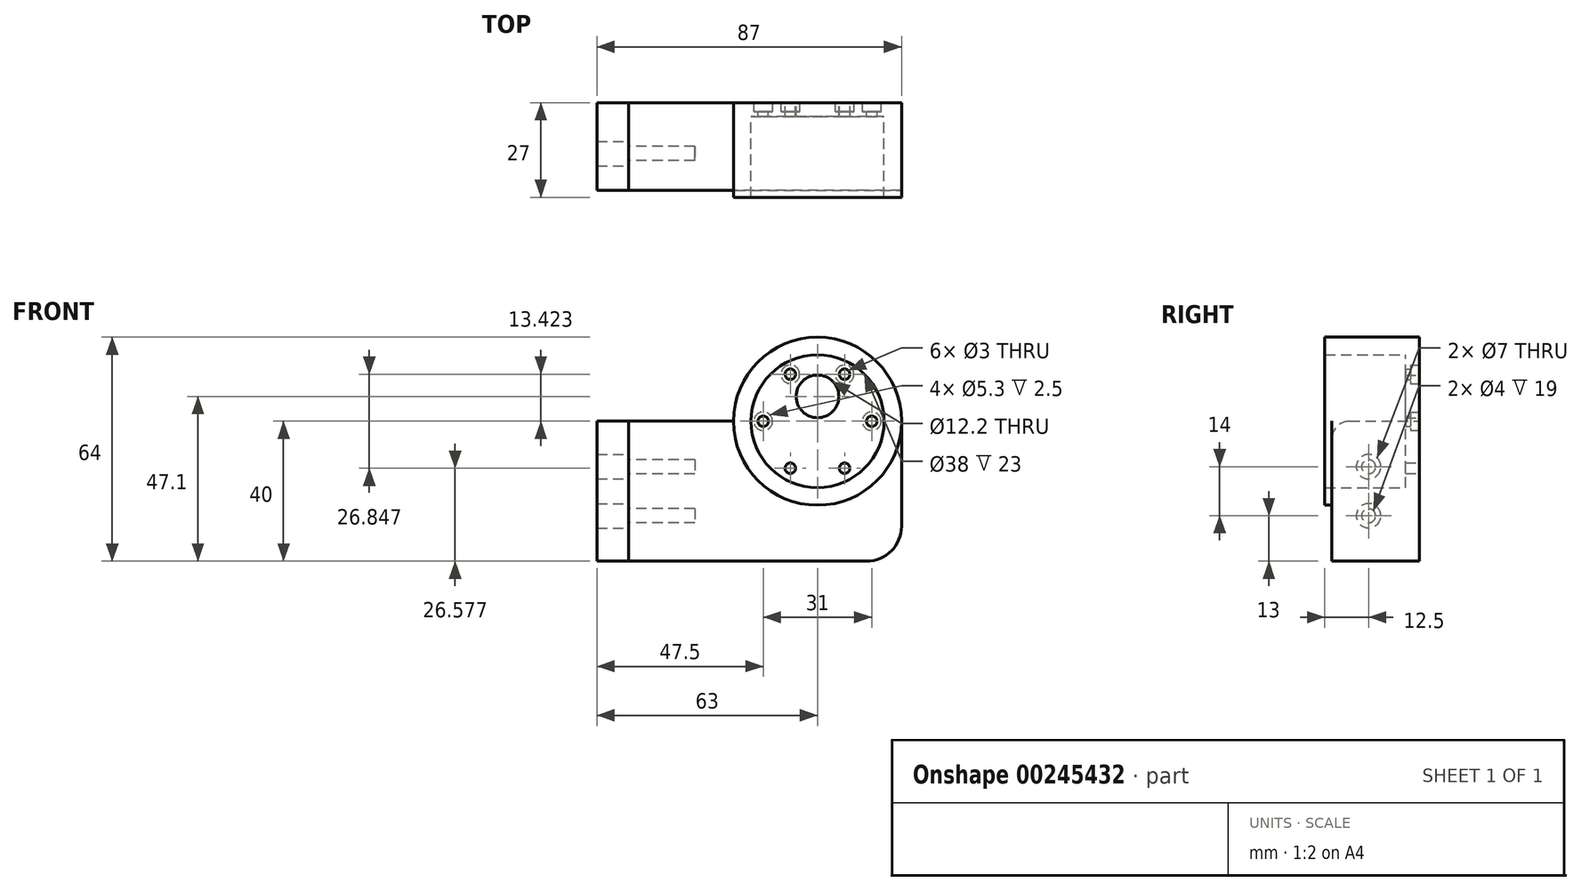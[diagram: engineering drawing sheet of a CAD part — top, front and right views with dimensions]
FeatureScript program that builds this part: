
annotation { "Feature Type Name" : "Feature", "Feature Type Description" : "" }
export const myFeature = defineFeature(function(context is Context, id is Id, definition is map)
    precondition{}
    {
        {
            var Q0;
            Q0=qCreatedBy(makeId("Front.planeOp"),FACE);
            var sketch = newSketch(context, id + "F0", { "sketchPlane" : qUnion([Q0])});
            skCircle(sketch, "E0", {"center": v(0, 0) * mm, "radius": 19 * mm});
            skCircle(sketch, "E1", {"center": v(0, 7.1) * mm, "radius": 6.1 * mm});
            skLineSegment(sketch, "E2", {"start": v(0, 0) * mm, "end": v(15.5, 0) * mm});
            skCircle(sketch, "E3", {"center": v(15.5, 0) * mm, "radius": 1.5 * mm});
            skCircle(sketch, "E4.1.0", {"center": v(7.75, 13.42) * mm, "radius": 1.5 * mm});
            skCircle(sketch, "E4.2.0", {"center": v(-7.75, 13.42) * mm, "radius": 1.5 * mm});
            skCircle(sketch, "E4.3.0", {"center": v(-15.5, 0) * mm, "radius": 1.5 * mm});
            skCircle(sketch, "E4.4.0", {"center": v(-7.75, -13.42) * mm, "radius": 1.5 * mm});
            skCircle(sketch, "E4.5.0", {"center": v(7.75, -13.42) * mm, "radius": 1.5 * mm});
            skSolve(sketch);
        }
        {
            var Q0;
            Q0=qSketchRegion(id+"F0",true);
            extrude(context, id + "F1", {"entities" : qUnion([Q0]), "depth" : 4 * mm});
        }
        {
            var Q0;
            Q0=qCreatedBy(makeId("Front.planeOp"),FACE);
            var sketch = newSketch(context, id + "F2", { "sketchPlane" : qUnion([Q0])});
            skCircle(sketch, "E5", {"center": v(0, 0) * mm, "radius": 19 * mm});
            skCircle(sketch, "E6", {"center": v(0, 0) * mm, "radius": 24 * mm});
            skSolve(sketch);
        }
        {
            var Q0;
            Q0=qSketchRegion(id+"F2",true);
            extrude(context, id + "F3", {"entities" : qUnion([Q0]), "operationType" : NewBodyOperationType.ADD, "depth" : 27 * mm});
        }
        {
            var Q0;
            Q0=makeQuery(id+"F3.boolean.opBoolean","MERGE",FACE,{"derivedFrom":[makeQuery(id+"F1.opExtrude","CAP_FACE",FACE,{"disambiguationData":[OSD([sQuery(id+"F0.wireOp",EDGE,"E0"),sQuery(id+"F0.wireOp",EDGE,"E1"),sQuery(id+"F0.wireOp",EDGE,"E3"),sQuery(id+"F0.wireOp",EDGE,"E4.1.0"),sQuery(id+"F0.wireOp",EDGE,"E4.2.0"),sQuery(id+"F0.wireOp",EDGE,"E4.3.0"),sQuery(id+"F0.wireOp",EDGE,"E4.4.0"),sQuery(id+"F0.wireOp",EDGE,"E4.5.0")])],"isStart":true}),makeQuery(id+"F3.opExtrude","CAP_FACE",FACE,{"disambiguationData":[OSD([sQuery(id+"F2.wireOp",EDGE,"E5"),sQuery(id+"F2.wireOp",EDGE,"E6")])],"isStart":true})]});
            var sketch = newSketch(context, id + "F4", { "sketchPlane" : qUnion([Q0])});
            skLineSegment(sketch, "E7", {"start": v(24, 0) * mm, "end": v(24, -40) * mm});
            skLineSegment(sketch, "E8", {"start": v(24, -40) * mm, "end": v(0, -40) * mm});
            skLineSegment(sketch, "E9", {"start": v(-24, 0) * mm, "end": v(-24, -40) * mm});
            skLineSegment(sketch, "E10", {"start": v(-24, -40) * mm, "end": v(0, -40) * mm});
            skArc(sketch, "E11", {"start": v(-24, 0) * mm, "mid": v(0, -24) * mm, "end": v(24, 0) * mm});
            skSolve(sketch);
        }
        {
            var Q0;
            Q0=qSketchRegion(id+"F4",true);
            extrude(context, id + "F5", {"entities" : qUnion([Q0]), "operationType" : NewBodyOperationType.ADD, "oppositeDirection" : true, "depth" : 25 * mm});
        }
        {
            var Q0;
            Q0=makeQuery(id+"F5.boolean.opBoolean","MERGE",FACE,{"derivedFrom":[makeQuery(id+"F3.boolean.opBoolean","MERGE",FACE,{"derivedFrom":[makeQuery(id+"F1.opExtrude","CAP_FACE",FACE,{"disambiguationData":[OSD([sQuery(id+"F0.wireOp",EDGE,"E0"),sQuery(id+"F0.wireOp",EDGE,"E1"),sQuery(id+"F0.wireOp",EDGE,"E3"),sQuery(id+"F0.wireOp",EDGE,"E4.1.0"),sQuery(id+"F0.wireOp",EDGE,"E4.2.0"),sQuery(id+"F0.wireOp",EDGE,"E4.3.0"),sQuery(id+"F0.wireOp",EDGE,"E4.4.0"),sQuery(id+"F0.wireOp",EDGE,"E4.5.0")])],"isStart":true}),makeQuery(id+"F3.opExtrude","CAP_FACE",FACE,{"disambiguationData":[OSD([sQuery(id+"F2.wireOp",EDGE,"E5"),sQuery(id+"F2.wireOp",EDGE,"E6")])],"isStart":true})]}),makeQuery(id+"F5.opExtrude","CAP_FACE",FACE,{"disambiguationData":[OSD([sQuery(id+"F4.wireOp",EDGE,"E7"),sQuery(id+"F4.wireOp",EDGE,"E8"),sQuery(id+"F4.wireOp",EDGE,"E9"),sQuery(id+"F4.wireOp",EDGE,"E10"),sQuery(id+"F4.wireOp",EDGE,"E11")])],"isStart":true})]});
            var sketch = newSketch(context, id + "F6", { "sketchPlane" : qUnion([Q0])});
            skCircle(sketch, "E12", {"center": v(-7.75, 13.42) * mm, "radius": 2.65 * mm});
            skCircle(sketch, "E13", {"center": v(7.75, 13.42) * mm, "radius": 2.65 * mm});
            skCircle(sketch, "E14", {"center": v(-15.5, 0) * mm, "radius": 2.65 * mm});
            skCircle(sketch, "E15", {"center": v(15.5, 0) * mm, "radius": 2.65 * mm});
            skSolve(sketch);
        }
        {
            var Q0;
            Q0=qSketchRegion(id+"F6",true);
            extrude(context, id + "F7", {"entities" : qUnion([Q0]), "operationType" : NewBodyOperationType.REMOVE, "oppositeDirection" : true, "depth" : 2.5 * mm});
        }
        {
            var Q0;
            Q0=makeQuery(id+"F5.opExtrude","SWEPT_FACE",FACE,{"disambiguationData":[OSD([sQuery(id+"F4.wireOp",EDGE,"E7")])]});
            var sketch = newSketch(context, id + "F8", { "sketchPlane" : qUnion([Q0])});
            skLineSegment(sketch, "E16.bottom", {"start": v(0, 0) * mm, "end": v(25, 0) * mm});
            skLineSegment(sketch, "E16.top", {"start": v(0, -40) * mm, "end": v(25, -40) * mm});
            skLineSegment(sketch, "E16.left", {"start": v(0, 0) * mm, "end": v(0, -40) * mm});
            skLineSegment(sketch, "E16.right", {"start": v(25, 0) * mm, "end": v(25, -40) * mm});
            skSolve(sketch);
        }
        {
            var Q0;
            Q0=qSketchRegion(id+"F8",true);
            extrude(context, id + "F9", {"entities" : qUnion([Q0]), "operationType" : NewBodyOperationType.ADD, "depth" : 30 * mm});
        }
        {
            var Q0;
            Q0=makeQuery(id+"F9.opExtrude","SWEPT_EDGE",EDGE,{"disambiguationData":[OSD([sQuery(id+"F8.wireOp",EDGE,"E16.bottom"),sQuery(id+"F8.wireOp",EDGE,"E16.right")])]});
            fillet(context, id + "F10", {"entities" : qUnion([Q0]), "radius" : 5 * mm, "tangentPropagation" : true, "allowEdgeOverflow" : false});
        }
        {
            var Q0;
            Q0=makeQuery(id+"F5.opExtrude","SWEPT_EDGE",EDGE,{"disambiguationData":[OSD([sQuery(id+"F4.wireOp",EDGE,"E9"),sQuery(id+"F4.wireOp",EDGE,"E10")])]});
            fillet(context, id + "F11", {"entities" : qUnion([Q0]), "radius" : 10 * mm, "tangentPropagation" : true, "allowEdgeOverflow" : false});
        }
        {
            var Q0;
            Q0=makeQuery(id+"F9.opExtrude","CAP_FACE",FACE,{"disambiguationData":[OSD([sQuery(id+"F8.wireOp",EDGE,"E16.bottom"),sQuery(id+"F8.wireOp",EDGE,"E16.top"),sQuery(id+"F8.wireOp",EDGE,"E16.left"),sQuery(id+"F8.wireOp",EDGE,"E16.right")])],"isStart":false});
            var sketch = newSketch(context, id + "F12", { "sketchPlane" : qUnion([Q0])});
            skLineSegment(sketch, "E17", {"start": v(25, -40) * mm, "end": v(4, -40) * mm});
            skLineSegment(sketch, "E18", {"start": v(14.5, -40) * mm, "end": v(14.5, 0) * mm});
            skLineSegment(sketch, "E19", {"start": v(14.5, 0) * mm, "end": v(14.5, -13) * mm});
            skLineSegment(sketch, "E20", {"start": v(14.5, -40) * mm, "end": v(14.5, -27) * mm});
            skCircle(sketch, "E21", {"center": v(14.5, -13) * mm, "radius": 2 * mm});
            skCircle(sketch, "E22", {"center": v(14.5, -27) * mm, "radius": 2 * mm});
            skSolve(sketch);
        }
        {
            var Q0;
            Q0=qSketchRegion(id+"F12",true);
            extrude(context, id + "F13", {"entities" : qUnion([Q0]), "operationType" : NewBodyOperationType.REMOVE, "oppositeDirection" : true, "depth" : 19 * mm});
        }
        {
            var Q0;
            Q0=makeQuery(id+"F9.opExtrude","CAP_FACE",FACE,{"disambiguationData":[OSD([sQuery(id+"F8.wireOp",EDGE,"E16.bottom"),sQuery(id+"F8.wireOp",EDGE,"E16.top"),sQuery(id+"F8.wireOp",EDGE,"E16.left"),sQuery(id+"F8.wireOp",EDGE,"E16.right")])],"isStart":false});
            var sketch = newSketch(context, id + "F14", { "sketchPlane" : qUnion([Q0])});
            skLineSegment(sketch, "E23.0", {"start": v(0, 0) * mm, "end": v(0, -40) * mm});
            skLineSegment(sketch, "E24.0", {"start": v(25, -5) * mm, "end": v(25, -40) * mm});
            skArc(sketch, "E25.0", {"start": v(25, -5) * mm, "mid": v(23.54, -1.46) * mm, "end": v(20, 0) * mm});
            skLineSegment(sketch, "E26.0", {"start": v(20, 0) * mm, "end": v(0, 0) * mm});
            skLineSegment(sketch, "E27.0", {"start": v(25, -40) * mm, "end": v(0, -40) * mm});
            skCircle(sketch, "E28", {"center": v(14.5, -13) * mm, "radius": 3.5 * mm});
            skCircle(sketch, "E29", {"center": v(14.5, -27) * mm, "radius": 3.5 * mm});
            skSolve(sketch);
        }
        {
            var Q0;
            Q0 = qSketchRegion(id + "F14", true);
            extrude(context, id + "F15", {"entities" : qUnion([Q0]), "depth" : 9 * mm, "offsetDistance" : 25 * mm});
        }
    });
